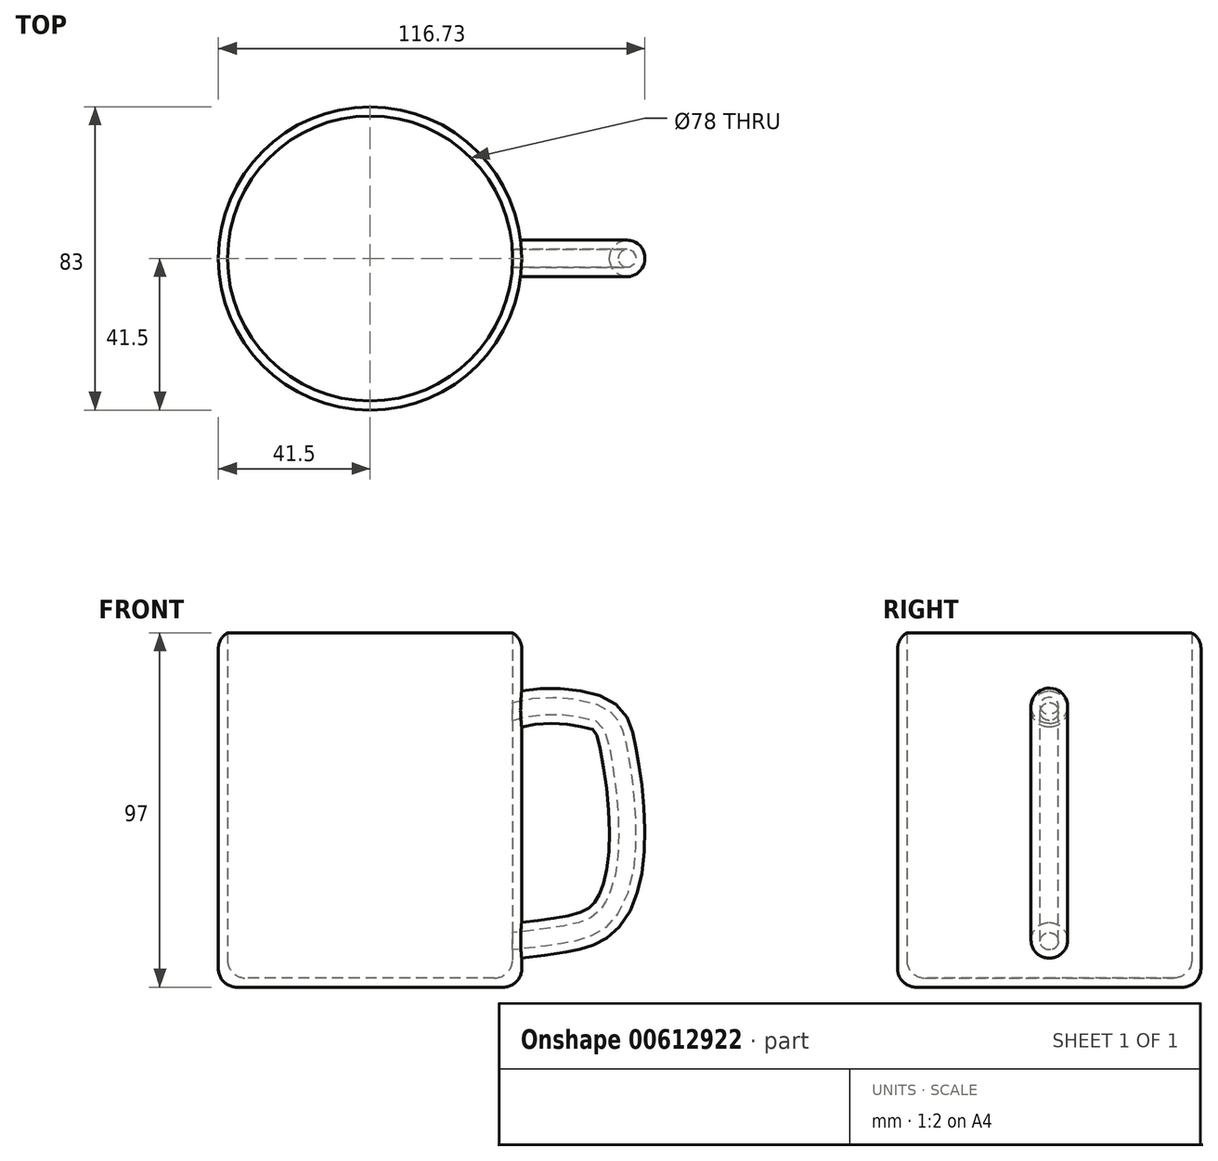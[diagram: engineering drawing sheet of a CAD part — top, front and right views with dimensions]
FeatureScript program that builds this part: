
annotation { "Feature Type Name" : "Feature", "Feature Type Description" : "" }
export const myFeature = defineFeature(function(context is Context, id is Id, definition is map)
    precondition{}
    {
        {
            var Q0;
            Q0=qCreatedBy(makeId("Top.planeOp"),FACE);
            var sketch = newSketch(context, id + "F0", { "sketchPlane" : qUnion([Q0])});
            skCircle(sketch, "E0", {"center": v(0, 0) * mm, "radius": 41.5 * mm});
            skSolve(sketch);
        }
        {
            var Q0;
            Q0 = qSketchRegion(id + "F0", true);
            extrude(context, id + "F1", {"entities" : qUnion([Q0]), "depth" : 97 * mm, "offsetDistance" : 25 * mm});
        }
        {
            var Q0;
            Q0=qCreatedBy(makeId("Front.planeOp"),FACE);
            var sketch = newSketch(context, id + "F2", { "sketchPlane" : qUnion([Q0])});
            skFitSpline(sketch, "E1", {"points": [v(31.56, 74.64) * mm, v(45.46, 78.7) * mm, v(64.66, 75.61) * mm, v(69.91, 65) * mm, v(71.94, 34.71) * mm, v(64.82, 17.2) * mm, v(53.1, 12.48) * mm, v(36.13, 10.36) * mm], "startDerivative": vector(95.75, 40.16) * mm, "endDerivative": vector(-124.16, -12.5) * mm});
            skSolve(sketch);
        }
        {
            var Q0;
            Q0=qCreatedBy(makeId("Right.planeOp"),FACE);
            cPlane(context, id + "F3", {"entities" : qUnion([Q0]), "cplaneType" : CPlaneType.OFFSET, "offset" : 40.2 * mm, "width" : 150 * mm, "height" : 150 * mm});
        }
        {
            var Q0;
            Q0=qCreatedBy(id+"F3.planeOp",FACE);
            var sketch = newSketch(context, id + "F4", { "sketchPlane" : qUnion([Q0])});
            skCircle(sketch, "E2", {"center": v(0, 75.8) * mm, "radius": 5 * mm});
            skSolve(sketch);
        }
        {
            var Q0;
            Q0 = qSketchRegion(id + "F4", true);
            var Q1;
            Q1=sQuery(id+"F2.wireOp",EDGE,"E1");
            sweep(context, id + "F5", {"operationType" : NewBodyOperationType.ADD, "profiles" : qUnion([Q0]), "path" : qUnion([Q1])});
        }
        {
            var Q0;
            Q0=makeQuery(id+"F1.opExtrude","CAP_FACE",FACE,{"disambiguationData":[OSD([sQuery(id+"F0.wireOp",EDGE,"E0")])],"isStart":false});
            shell(context, id + "F6", {"entities" : qUnion([Q0]), "thickness" : 2.5 * mm});
        }
        {
            var Q0;
            Q0=makeQuery(id+"F1.opExtrude","CAP_EDGE",EDGE,{"disambiguationData":[OSD([sQuery(id+"F0.wireOp",EDGE,"E0")])],"isStart":false});
            var Q1;
            {var subQ0=sQuery(id+"F0.wireOp",EDGE,"E0");Q1=makeQuery(id+"F6.opShell","OFFSET_FACE",FACE,{"disambiguationData":[OSD([subQ0]),TDD([makeQuery(id+"F1.opExtrude","CAP_FACE",FACE,{"disambiguationData":[OSD([subQ0])],"isStart":true})])]});}
            var Q2;
            Q2=makeQuery(id+"F1.opExtrude","CAP_EDGE",EDGE,{"disambiguationData":[OSD([sQuery(id+"F0.wireOp",EDGE,"E0")])],"isStart":true});
            fillet(context, id + "F7", {"entities" : qUnion([Q0, Q1, Q2]), "radius" : 5 * mm, "tangentPropagation" : true, "allowEdgeOverflow" : false});
        }
    });
